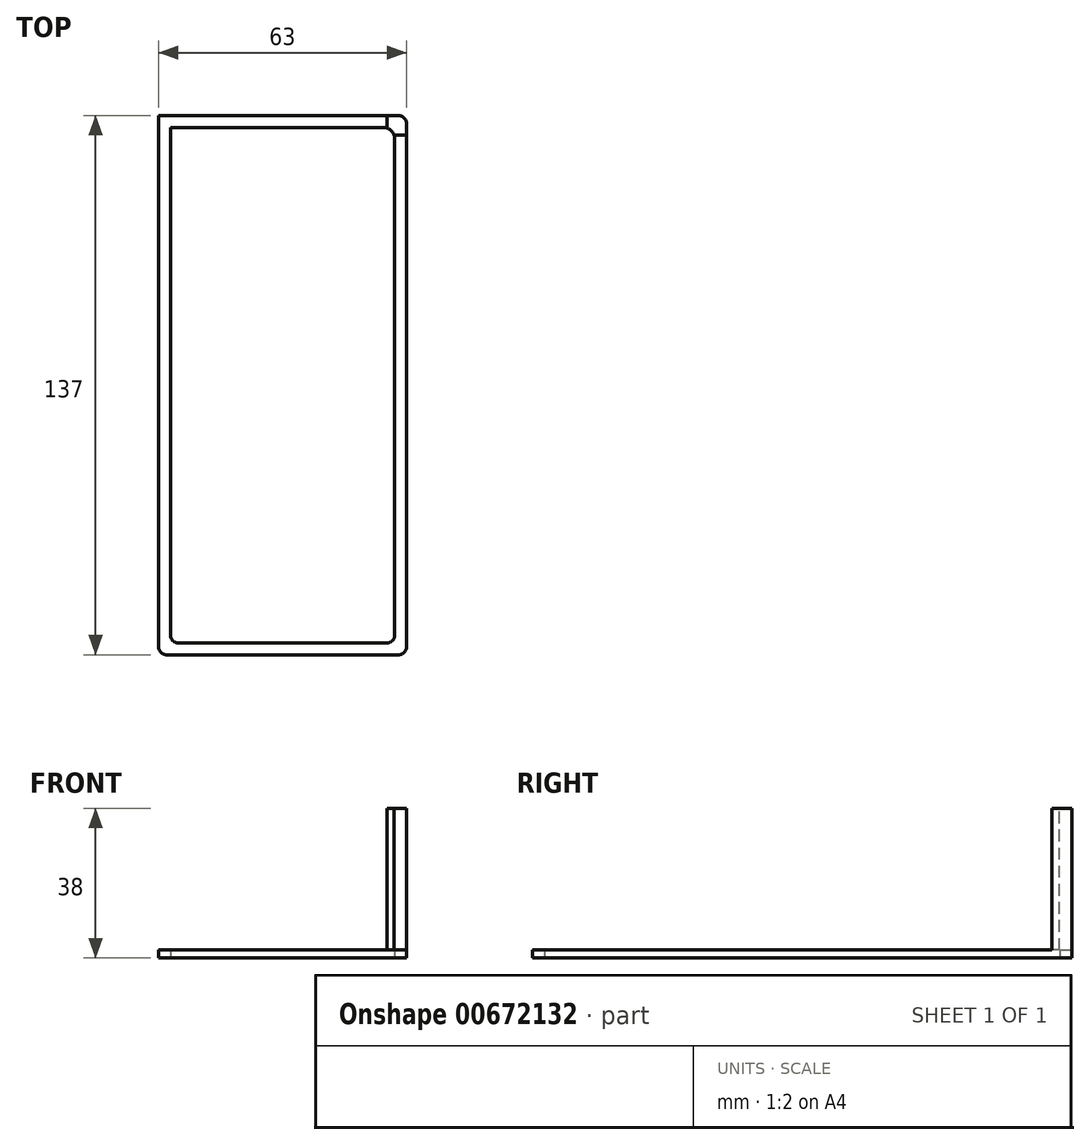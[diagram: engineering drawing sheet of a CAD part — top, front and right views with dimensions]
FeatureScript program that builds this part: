
annotation { "Feature Type Name" : "Feature", "Feature Type Description" : "" }
export const myFeature = defineFeature(function(context is Context, id is Id, definition is map)
    precondition{}
    {
        {
            var Q0;
            Q0=qCreatedBy(makeId("Top.planeOp"),FACE);
            var sketch = newSketch(context, id + "F0", { "sketchPlane" : qUnion([Q0])});
            skLineSegment(sketch, "E0.bottom", {"start": v(-31.5, 68.5) * mm, "end": v(31.5, 68.5) * mm});
            skLineSegment(sketch, "E0.top", {"start": v(-31.5, -68.5) * mm, "end": v(31.5, -68.5) * mm});
            skLineSegment(sketch, "E0.left", {"start": v(-31.5, 68.5) * mm, "end": v(-31.5, -68.5) * mm});
            skLineSegment(sketch, "E0.right", {"start": v(31.5, 68.5) * mm, "end": v(31.5, -68.5) * mm});
            skPoint(sketch, "E0.middle", {"position": v(0, 0) * mm});
            skLineSegment(sketch, "E1.0", {"start": v(-28.5, 65.5) * mm, "end": v(-28.5, -65.5) * mm});
            skLineSegment(sketch, "E1.1", {"start": v(-28.5, 65.5) * mm, "end": v(28.5, 65.5) * mm});
            skLineSegment(sketch, "E1.2", {"start": v(28.5, 65.5) * mm, "end": v(28.5, -65.5) * mm});
            skLineSegment(sketch, "E1.3", {"start": v(-28.5, -65.5) * mm, "end": v(28.5, -65.5) * mm});
            skSolve(sketch);
        }
        {
            var Q0;
            Q0=makeQuery(id+"F0.imprint","IMPRINT",FACE,{"disambiguationData":[TD([[makeQuery(id+"F0.imprint","IMPRINT",EDGE,{"derivedFrom":sQuery(id+"F0.wireOp",EDGE,"E0.bottom")}),-1.0]])]});
            extrude(context, id + "F1", {"entities" : qUnion([Q0]), "depth" : 2 * mm, "offsetDistance" : 25 * mm});
        }
        {
            var Q0;
            Q0=qCreatedBy(makeId("Front.planeOp"),FACE);
            var sketch = newSketch(context, id + "F2", { "sketchPlane" : qUnion([Q0])});
            skLineSegment(sketch, "E2.0", {"start": v(-31.5, 0) * mm, "end": v(31.5, 0) * mm});
            skLineSegment(sketch, "E3", {"start": v(-31.5, 0) * mm, "end": v(-31.5, 38) * mm});
            skLineSegment(sketch, "E4", {"start": v(-31.5, 38) * mm, "end": v(31.5, 38) * mm});
            skLineSegment(sketch, "E5", {"start": v(31.5, 38) * mm, "end": v(31.5, 0) * mm});
            skSolve(sketch);
        }
        {
            var Q0;
            Q0=makeQuery(id+"F1.opExtrude","CAP_FACE",FACE,{"disambiguationData":[OSD([sQuery(id+"F0.wireOp",EDGE,"E0.bottom"),sQuery(id+"F0.wireOp",EDGE,"E0.top"),sQuery(id+"F0.wireOp",EDGE,"E0.left"),sQuery(id+"F0.wireOp",EDGE,"E0.right")])],"isStart":false});
            var sketch = newSketch(context, id + "F3", { "sketchPlane" : qUnion([Q0])});
            skLineSegment(sketch, "E6.0.0", {"start": v(-31.5, 68.5) * mm, "end": v(-31.5, -68.5) * mm});
            skLineSegment(sketch, "E6.0.1", {"start": v(-31.5, -68.5) * mm, "end": v(31.5, -68.5) * mm});
            skLineSegment(sketch, "E6.0.2", {"start": v(31.5, -68.5) * mm, "end": v(31.5, 68.5) * mm});
            skLineSegment(sketch, "E6.0.3", {"start": v(31.5, 68.5) * mm, "end": v(-31.5, 68.5) * mm});
            skLineSegment(sketch, "E7.0", {"start": v(-28.5, 65.5) * mm, "end": v(-28.5, -65.5) * mm});
            skLineSegment(sketch, "E7.1", {"start": v(28.5, 65.5) * mm, "end": v(-28.5, 65.5) * mm});
            skLineSegment(sketch, "E7.2", {"start": v(28.5, -65.5) * mm, "end": v(28.5, 65.5) * mm});
            skLineSegment(sketch, "E7.3", {"start": v(-28.5, -65.5) * mm, "end": v(28.5, -65.5) * mm});
            skLineSegment(sketch, "E8", {"start": v(-31.5, 68.5) * mm, "end": v(-31.5, 63.5) * mm});
            skLineSegment(sketch, "E9", {"start": v(-31.5, 63.5) * mm, "end": v(-26.5, 63.5) * mm});
            skLineSegment(sketch, "E10", {"start": v(-26.5, 63.5) * mm, "end": v(-26.5, 68.5) * mm});
            skLineSegment(sketch, "E11", {"start": v(0, 0) * mm, "end": v(0, 21.64) * mm, "construction": true});
            skLineSegment(sketch, "E12", {"start": v(1.27, 0) * mm, "end": v(10.35, 0) * mm, "construction": true});
            skLineSegment(sketch, "E13.MirrorCS", {"start": v(31.5, 63.5) * mm, "end": v(26.5, 63.5) * mm});
            skLineSegment(sketch, "E14.MirrorCS", {"start": v(26.5, 63.5) * mm, "end": v(26.5, 68.5) * mm});
            skLineSegment(sketch, "E15.MirrorCS", {"start": v(-31.5, -63.5) * mm, "end": v(-26.5, -63.5) * mm});
            skLineSegment(sketch, "E16.MirrorCS", {"start": v(-26.5, -63.5) * mm, "end": v(-26.5, -68.5) * mm});
            skLineSegment(sketch, "E17.MirrorCS", {"start": v(26.5, -63.5) * mm, "end": v(26.5, -68.5) * mm});
            skLineSegment(sketch, "E18.MirrorCS", {"start": v(31.5, -63.5) * mm, "end": v(26.5, -63.5) * mm});
            skSolve(sketch);
        }
        {
            var Q0;
            {var subQ9=sQuery(id+"F3.wireOp",EDGE,"E8");Q0=makeQuery(id+"F3.imprint","IMPRINT",FACE,{"disambiguationData":[TD([[makeQuery(id+"F3.imprint","IMPRINT",EDGE,{"derivedFrom":subQ9}),1.0]])]});}
            var Q1;
            {var subQ7=sQuery(id+"F3.wireOp",EDGE,"E6.0.3");var subQ8=sQuery(id+"F3.wireOp",EDGE,"E6.0.2");var subQ9=makeQuery(id+"F3.imprint","INTERSECT",VERTEX,{"derivedFrom":[subQ8,subQ7]});Q1=makeQuery(id+"F3.imprint","IMPRINT",FACE,{"disambiguationData":[TD([[makeQuery(id+"F3.imprint","IMPRINT",EDGE,{"disambiguationData":[TD([[subQ9,-1.0]])],"derivedFrom":subQ8}),-1.0]])]});}
            var Q2;
            Q2=sQuery(id+"F2.wireOp",VERTEX,"E4.start");
            extrude(context, id + "F4", {"entities" : qUnion([Q0, Q1]), "operationType" : NewBodyOperationType.ADD, "endBound" : BoundingType.UP_TO_VERTEX, "depth" : 25 * mm, "endBoundEntityVertex" : qUnion([Q2]), "offsetDistance" : 25 * mm});
        }
        {
            var Q0;
            Q0=makeQuery(id+"F4.boolean.opBoolean","MERGE",EDGE,{"derivedFrom":[makeQuery(id+"F1.opExtrude","SWEPT_EDGE",EDGE,{"disambiguationData":[OSD([sQuery(id+"F0.wireOp",EDGE,"E1.0"),sQuery(id+"F0.wireOp",EDGE,"E1.1")])]}),makeQuery(id+"F4.opExtrude","SWEPT_EDGE",EDGE,{"disambiguationData":[OSD([sQuery(id+"F3.wireOp",EDGE,"E7.0"),sQuery(id+"F3.wireOp",EDGE,"E7.1")])]})]});
            var Q1;
            Q1=makeQuery(id+"F4.boolean.opBoolean","MERGE",EDGE,{"derivedFrom":[makeQuery(id+"F1.opExtrude","SWEPT_EDGE",EDGE,{"disambiguationData":[OSD([sQuery(id+"F0.wireOp",EDGE,"E1.1"),sQuery(id+"F0.wireOp",EDGE,"E1.2")])]}),makeQuery(id+"F4.opExtrude","SWEPT_EDGE",EDGE,{"disambiguationData":[OSD([sQuery(id+"F3.wireOp",EDGE,"E7.1"),sQuery(id+"F3.wireOp",EDGE,"E7.2")])]})]});
            fillet(context, id + "F5", {"entities" : qUnion([Q0, Q1]), "radius" : 3 * mm, "tangentPropagation" : true, "allowEdgeOverflow" : false});
        }
        {
            var Q0;
            Q0=makeQuery(id+"F4.boolean.opBoolean","MERGE",EDGE,{"derivedFrom":[makeQuery(id+"F1.opExtrude","SWEPT_EDGE",EDGE,{"disambiguationData":[OSD([sQuery(id+"F0.wireOp",EDGE,"E0.bottom"),sQuery(id+"F0.wireOp",EDGE,"E0.left")])]}),makeQuery(id+"F4.opExtrude","SWEPT_EDGE",EDGE,{"disambiguationData":[OSD([sQuery(id+"F3.wireOp",EDGE,"E6.0.3"),sQuery(id+"F3.wireOp",EDGE,"E8")])]})]});
            var Q1;
            Q1=makeQuery(id+"F4.boolean.opBoolean","MERGE",EDGE,{"derivedFrom":[makeQuery(id+"F1.opExtrude","SWEPT_EDGE",EDGE,{"disambiguationData":[OSD([sQuery(id+"F0.wireOp",EDGE,"E0.bottom"),sQuery(id+"F0.wireOp",EDGE,"E0.right")])]}),makeQuery(id+"F4.opExtrude","SWEPT_EDGE",EDGE,{"disambiguationData":[OSD([sQuery(id+"F3.wireOp",EDGE,"E6.0.2"),sQuery(id+"F3.wireOp",EDGE,"E6.0.3")])]})]});
            var Q2;
            Q2=makeQuery(id+"F1.opExtrude","SWEPT_EDGE",EDGE,{"disambiguationData":[OSD([sQuery(id+"F0.wireOp",EDGE,"E0.top"),sQuery(id+"F0.wireOp",EDGE,"E0.right")])]});
            var Q3;
            Q3=makeQuery(id+"F1.opExtrude","SWEPT_EDGE",EDGE,{"disambiguationData":[OSD([sQuery(id+"F0.wireOp",EDGE,"E0.top"),sQuery(id+"F0.wireOp",EDGE,"E0.left")])]});
            var Q4;
            Q4=makeQuery(id+"F1.opExtrude","SWEPT_EDGE",EDGE,{"disambiguationData":[OSD([sQuery(id+"F0.wireOp",EDGE,"E1.2"),sQuery(id+"F0.wireOp",EDGE,"E1.3")])]});
            var Q5;
            Q5=makeQuery(id+"F1.opExtrude","SWEPT_EDGE",EDGE,{"disambiguationData":[OSD([sQuery(id+"F0.wireOp",EDGE,"E1.0"),sQuery(id+"F0.wireOp",EDGE,"E1.3")])]});
            fillet(context, id + "F6", {"entities" : qUnion([Q0, Q1, Q2, Q3, Q4, Q5]), "radius" : 2 * mm, "tangentPropagation" : true, "allowEdgeOverflow" : false});
        }
    });
